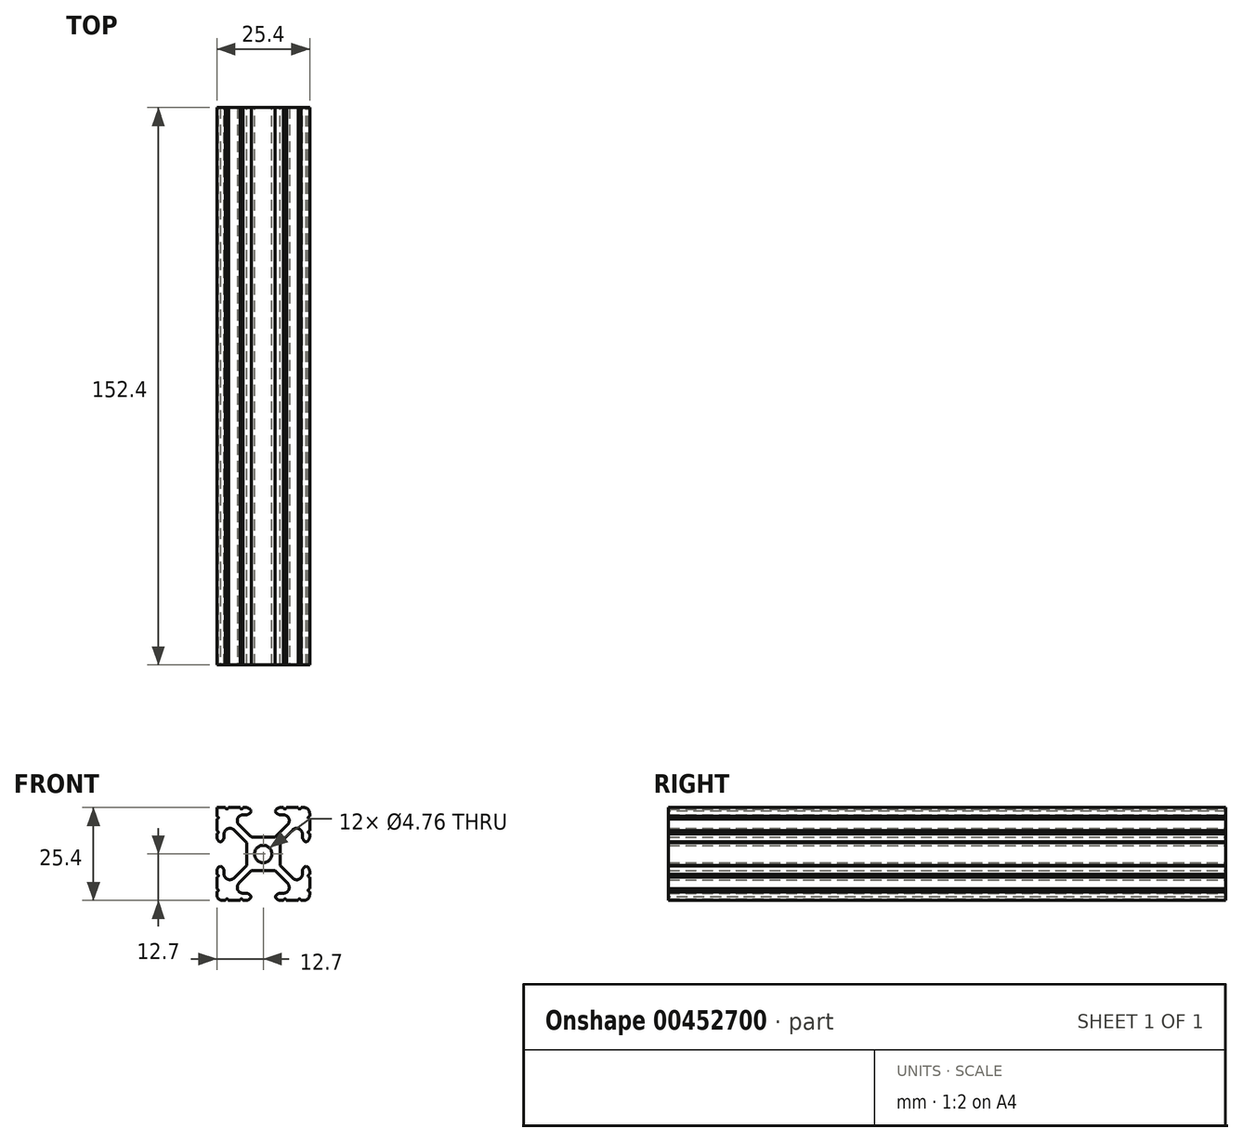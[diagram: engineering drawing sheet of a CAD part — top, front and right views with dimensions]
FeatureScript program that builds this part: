
annotation { "Feature Type Name" : "Feature", "Feature Type Description" : "" }
export const myFeature = defineFeature(function(context is Context, id is Id, definition is map)
    precondition{}
    {
        {
            var Q0;
            Q0=qCreatedBy(makeId("Front.planeOp"),FACE);
            var sketch = newSketch(context, id + "F0", { "sketchPlane" : qUnion([Q0])});
            skCircle(sketch, "E0", {"center": v(0, 0) * mm, "radius": 2.38 * mm});
            skLineSegment(sketch, "E1.bottom", {"start": v(-12.7, 12.7) * mm, "end": v(12.7, 12.7) * mm});
            skLineSegment(sketch, "E1.top", {"start": v(-12.7, -12.7) * mm, "end": v(12.7, -12.7) * mm});
            skLineSegment(sketch, "E1.left", {"start": v(-12.7, 12.7) * mm, "end": v(-12.7, -12.7) * mm});
            skLineSegment(sketch, "E1.right", {"start": v(12.7, 12.7) * mm, "end": v(12.7, -12.7) * mm});
            skPoint(sketch, "E2", {"position": v(0, 12.7) * mm});
            skLineSegment(sketch, "E3", {"start": v(0, 12.7) * mm, "end": v(-3.18, 12.7) * mm});
            skLineSegment(sketch, "E4", {"start": v(0, 12.7) * mm, "end": v(3.17, 12.7) * mm});
            skLineSegment(sketch, "E5", {"start": v(-3.18, 12.7) * mm, "end": v(-3.18, 10.72) * mm});
            skPoint(sketch, "E6", {"position": v(-12.7, 0) * mm});
            skLineSegment(sketch, "E7", {"start": v(-12.7, 0) * mm, "end": v(-12.7, 3.18) * mm});
            skLineSegment(sketch, "E8.MirrorCS", {"start": v(-12.7, 0) * mm, "end": v(-12.7, -3.18) * mm});
            skLineSegment(sketch, "E9", {"start": v(-12.7, 3.18) * mm, "end": v(-10.72, 3.18) * mm});
            skLineSegment(sketch, "E10.MirrorCS", {"start": v(-12.7, -3.18) * mm, "end": v(-10.72, -3.18) * mm});
            skLineSegment(sketch, "E11.MirrorCS", {"start": v(3.18, 12.7) * mm, "end": v(3.18, 10.72) * mm});
            skLineSegment(sketch, "E12.bottom", {"start": v(-12.7, 12.7) * mm, "end": v(-7.14, 12.7) * mm});
            skLineSegment(sketch, "E13", {"start": v(-3.18, 10.72) * mm, "end": v(-7.14, 10.72) * mm});
            skLineSegment(sketch, "E14", {"start": v(-10.72, 3.18) * mm, "end": v(-10.72, 7.14) * mm});
            skLineSegment(sketch, "E15", {"start": v(-12.7, 11.22) * mm, "end": v(-11.37, 12.7) * mm});
            skLineSegment(sketch, "E16", {"start": v(-0.7, -0.7) * mm, "end": v(-12.7, 11.22) * mm});
            skLineSegment(sketch, "E17", {"start": v(-11.37, 12.7) * mm, "end": v(0.7, 0.7) * mm});
            skLineSegment(sketch, "E18.MirrorCS", {"start": v(3.18, 10.72) * mm, "end": v(7.14, 10.72) * mm});
            skLineSegment(sketch, "E19.MirrorCS", {"start": v(10.72, 3.18) * mm, "end": v(10.72, 7.14) * mm});
            skLineSegment(sketch, "E20.MirrorCS", {"start": v(12.7, 3.18) * mm, "end": v(10.72, 3.18) * mm});
            skLineSegment(sketch, "E21.MirrorCS", {"start": v(0.7, -0.7) * mm, "end": v(12.7, 11.22) * mm});
            skLineSegment(sketch, "E22.MirrorCS", {"start": v(11.37, 12.7) * mm, "end": v(-0.7, 0.7) * mm});
            skLineSegment(sketch, "E23.MirrorCS", {"start": v(3.18, -10.72) * mm, "end": v(7.14, -10.72) * mm});
            skLineSegment(sketch, "E24.MirrorCS", {"start": v(3.18, -12.7) * mm, "end": v(3.18, -10.72) * mm});
            skLineSegment(sketch, "E25.MirrorCS", {"start": v(11.37, -12.7) * mm, "end": v(-0.7, -0.7) * mm});
            skLineSegment(sketch, "E26.MirrorCS", {"start": v(0.7, 0.7) * mm, "end": v(12.7, -11.22) * mm});
            skLineSegment(sketch, "E27.MirrorCS", {"start": v(10.72, -3.18) * mm, "end": v(10.72, -7.14) * mm});
            skLineSegment(sketch, "E28.MirrorCS", {"start": v(12.7, -3.18) * mm, "end": v(10.72, -3.18) * mm});
            skLineSegment(sketch, "E29.MirrorCS", {"start": v(-3.18, -12.7) * mm, "end": v(-3.18, -10.72) * mm});
            skLineSegment(sketch, "E30.MirrorCS", {"start": v(-3.18, -10.72) * mm, "end": v(-7.14, -10.72) * mm});
            skLineSegment(sketch, "E31.MirrorCS", {"start": v(-11.37, -12.7) * mm, "end": v(0.7, -0.7) * mm});
            skLineSegment(sketch, "E32.MirrorCS", {"start": v(-0.7, 0.7) * mm, "end": v(-12.7, -11.22) * mm});
            skLineSegment(sketch, "E33.MirrorCS", {"start": v(-10.72, -3.18) * mm, "end": v(-10.72, -7.14) * mm});
            skLineSegment(sketch, "E34.bottom", {"start": v(-4.56, 4.56) * mm, "end": v(4.56, 4.56) * mm});
            skLineSegment(sketch, "E34.top", {"start": v(-4.56, -4.56) * mm, "end": v(4.56, -4.56) * mm});
            skLineSegment(sketch, "E34.left", {"start": v(-4.56, 4.56) * mm, "end": v(-4.56, -4.56) * mm});
            skLineSegment(sketch, "E34.right", {"start": v(4.56, 4.56) * mm, "end": v(4.56, -4.56) * mm});
            skPoint(sketch, "E35", {"position": v(10.32, 12.7) * mm});
            skPoint(sketch, "E36", {"position": v(9.53, 12.7) * mm});
            skArc(sketch, "E37", {"start": v(9.53, 12.7) * mm, "mid": v(9.92, 12.3) * mm, "end": v(10.32, 12.7) * mm});
            skPoint(sketch, "E38", {"position": v(6.35, 12.7) * mm});
            skPoint(sketch, "E39", {"position": v(5.56, 12.7) * mm});
            skArc(sketch, "E40", {"start": v(5.56, 12.7) * mm, "mid": v(5.95, 12.3) * mm, "end": v(6.35, 12.7) * mm});
            skArc(sketch, "E41.MirrorCS", {"start": v(9.53, -12.7) * mm, "mid": v(9.92, -12.3) * mm, "end": v(10.32, -12.7) * mm});
            skArc(sketch, "E42.MirrorCS", {"start": v(5.56, -12.7) * mm, "mid": v(5.95, -12.3) * mm, "end": v(6.35, -12.7) * mm});
            skArc(sketch, "E43.MirrorCS", {"start": v(-5.56, -12.7) * mm, "mid": v(-5.95, -12.3) * mm, "end": v(-6.35, -12.7) * mm});
            skArc(sketch, "E44.MirrorCS", {"start": v(-9.53, -12.7) * mm, "mid": v(-9.92, -12.3) * mm, "end": v(-10.32, -12.7) * mm});
            skArc(sketch, "E45.MirrorCS", {"start": v(-5.56, 12.7) * mm, "mid": v(-5.95, 12.3) * mm, "end": v(-6.35, 12.7) * mm});
            skArc(sketch, "E46.MirrorCS", {"start": v(-9.53, 12.7) * mm, "mid": v(-9.92, 12.3) * mm, "end": v(-10.32, 12.7) * mm});
            skPoint(sketch, "E47", {"position": v(12.7, 10.32) * mm});
            skPoint(sketch, "E48", {"position": v(12.7, 9.53) * mm});
            skPoint(sketch, "E49", {"position": v(12.7, 6.35) * mm});
            skPoint(sketch, "E50", {"position": v(12.7, 5.56) * mm});
            skArc(sketch, "E51", {"start": v(12.7, 10.32) * mm, "mid": v(12.3, 9.92) * mm, "end": v(12.7, 9.53) * mm});
            skArc(sketch, "E52", {"start": v(12.7, 6.35) * mm, "mid": v(12.3, 5.95) * mm, "end": v(12.7, 5.56) * mm});
            skArc(sketch, "E53.MirrorCS", {"start": v(-12.7, 10.32) * mm, "mid": v(-12.3, 9.92) * mm, "end": v(-12.7, 9.53) * mm});
            skArc(sketch, "E54.MirrorCS", {"start": v(-12.7, 6.35) * mm, "mid": v(-12.3, 5.95) * mm, "end": v(-12.7, 5.56) * mm});
            skArc(sketch, "E55.MirrorCS", {"start": v(-12.7, -6.35) * mm, "mid": v(-12.3, -5.95) * mm, "end": v(-12.7, -5.56) * mm});
            skArc(sketch, "E56.MirrorCS", {"start": v(-12.7, -10.32) * mm, "mid": v(-12.3, -9.92) * mm, "end": v(-12.7, -9.53) * mm});
            skArc(sketch, "E57.MirrorCS", {"start": v(12.7, -6.35) * mm, "mid": v(12.3, -5.95) * mm, "end": v(12.7, -5.56) * mm});
            skArc(sketch, "E58.MirrorCS", {"start": v(12.7, -10.32) * mm, "mid": v(12.3, -9.92) * mm, "end": v(12.7, -9.53) * mm});
            skLineSegment(sketch, "E59", {"start": v(-10.72, 7.14) * mm, "end": v(-10.72, 9.25) * mm});
            skLineSegment(sketch, "E60", {"start": v(-7.14, 10.72) * mm, "end": v(-9.38, 10.72) * mm});
            skLineSegment(sketch, "E61", {"start": v(7.14, 10.72) * mm, "end": v(9.38, 10.72) * mm});
            skLineSegment(sketch, "E62", {"start": v(10.72, 7.14) * mm, "end": v(10.72, 9.25) * mm});
            skLineSegment(sketch, "E63", {"start": v(7.14, -10.72) * mm, "end": v(9.38, -10.72) * mm});
            skLineSegment(sketch, "E64", {"start": v(10.72, -7.14) * mm, "end": v(10.72, -9.25) * mm});
            skLineSegment(sketch, "E65", {"start": v(-10.72, -7.14) * mm, "end": v(-10.72, -9.25) * mm});
            skLineSegment(sketch, "E66", {"start": v(-7.14, -10.72) * mm, "end": v(-9.38, -10.72) * mm});
            skSolve(sketch);
        }
        {
            var Q0;
            {var subQ0=sQuery(id+"F0.wireOp",EDGE,"E22.MirrorCS");var subQ1=sQuery(id+"F0.wireOp",EDGE,"E0");var subQ2=makeQuery(id+"F0.imprint","INTERSECT",VERTEX,{"derivedFrom":[subQ1,subQ0]});Q0=makeQuery(id+"F0.imprint","IMPRINT",FACE,{"disambiguationData":[TD([[makeQuery(id+"F0.imprint","IMPRINT",EDGE,{"disambiguationData":[TD([[subQ2,-1.0]])],"derivedFrom":subQ1}),-1.0]])]});}
            var Q1;
            {var subQ3=sQuery(id+"F0.wireOp",EDGE,"E17");var subQ5=sQuery(id+"F0.wireOp",EDGE,"E0");var subQ6=makeQuery(id+"F0.imprint","INTERSECT",VERTEX,{"derivedFrom":[subQ5,subQ3]});Q1=makeQuery(id+"F0.imprint","IMPRINT",FACE,{"disambiguationData":[TD([[makeQuery(id+"F0.imprint","IMPRINT",EDGE,{"disambiguationData":[TD([[subQ6,-1.0]])],"derivedFrom":subQ5}),-1.0]])]});}
            var Q2;
            {var subQ0=sQuery(id+"F0.wireOp",EDGE,"E16");var subQ1=sQuery(id+"F0.wireOp",EDGE,"E0");var subQ2=makeQuery(id+"F0.imprint","INTERSECT",VERTEX,{"derivedFrom":[subQ1,subQ0]});Q2=makeQuery(id+"F0.imprint","IMPRINT",FACE,{"disambiguationData":[TD([[makeQuery(id+"F0.imprint","IMPRINT",EDGE,{"disambiguationData":[TD([[subQ2,-1.0]])],"derivedFrom":subQ1}),-1.0]])]});}
            var Q3;
            {var subQ5=sQuery(id+"F0.wireOp",EDGE,"E0");var subQ7=sQuery(id+"F0.wireOp",EDGE,"E32.MirrorCS");var subQ8=makeQuery(id+"F0.imprint","INTERSECT",VERTEX,{"derivedFrom":[subQ5,subQ7]});Q3=makeQuery(id+"F0.imprint","IMPRINT",FACE,{"disambiguationData":[TD([[makeQuery(id+"F0.imprint","IMPRINT",EDGE,{"disambiguationData":[TD([[subQ8,-1.0]])],"derivedFrom":subQ5}),-1.0]])]});}
            var Q4;
            {var subQ0=sQuery(id+"F0.wireOp",EDGE,"E31.MirrorCS");var subQ1=sQuery(id+"F0.wireOp",EDGE,"E0");var subQ2=makeQuery(id+"F0.imprint","INTERSECT",VERTEX,{"derivedFrom":[subQ1,subQ0]});Q4=makeQuery(id+"F0.imprint","IMPRINT",FACE,{"disambiguationData":[TD([[makeQuery(id+"F0.imprint","IMPRINT",EDGE,{"disambiguationData":[TD([[subQ2,-1.0]])],"derivedFrom":subQ1}),-1.0]])]});}
            var Q5;
            {var subQ3=sQuery(id+"F0.wireOp",EDGE,"E25.MirrorCS");var subQ6=sQuery(id+"F0.wireOp",EDGE,"E0");var subQ9=makeQuery(id+"F0.imprint","INTERSECT",VERTEX,{"derivedFrom":[subQ6,subQ3]});Q5=makeQuery(id+"F0.imprint","IMPRINT",FACE,{"disambiguationData":[TD([[makeQuery(id+"F0.imprint","IMPRINT",EDGE,{"disambiguationData":[TD([[subQ9,-1.0]])],"derivedFrom":subQ6}),-1.0]])]});}
            var Q6;
            {var subQ0=sQuery(id+"F0.wireOp",EDGE,"E21.MirrorCS");var subQ1=sQuery(id+"F0.wireOp",EDGE,"E0");var subQ2=makeQuery(id+"F0.imprint","INTERSECT",VERTEX,{"derivedFrom":[subQ1,subQ0]});Q6=makeQuery(id+"F0.imprint","IMPRINT",FACE,{"disambiguationData":[TD([[makeQuery(id+"F0.imprint","IMPRINT",EDGE,{"disambiguationData":[TD([[subQ2,1.0]])],"derivedFrom":subQ1}),-1.0]])]});}
            var Q7;
            {var subQ3=sQuery(id+"F0.wireOp",EDGE,"E22.MirrorCS");var subQ7=sQuery(id+"F0.wireOp",EDGE,"E0");var subQ8=makeQuery(id+"F0.imprint","INTERSECT",VERTEX,{"derivedFrom":[subQ7,subQ3]});Q7=makeQuery(id+"F0.imprint","IMPRINT",FACE,{"disambiguationData":[TD([[makeQuery(id+"F0.imprint","IMPRINT",EDGE,{"disambiguationData":[TD([[subQ8,1.0]])],"derivedFrom":subQ7}),-1.0]])]});}
            var Q8;
            {var subQ1=sQuery(id+"F0.wireOp",EDGE,"E1.right");var subQ6=sQuery(id+"F0.wireOp",EDGE,"E1.bottom");var subQ7=makeQuery(id+"F0.imprint","INTERSECT",VERTEX,{"derivedFrom":[subQ6,subQ1]});Q8=makeQuery(id+"F0.imprint","IMPRINT",FACE,{"disambiguationData":[TD([[makeQuery(id+"F0.imprint","IMPRINT",EDGE,{"disambiguationData":[TD([[subQ7,1.0]])],"derivedFrom":subQ6}),-1.0]])]});}
            var Q9;
            Q9=makeQuery(id+"F0.imprint","IMPRINT",FACE,{"disambiguationData":[TD([[makeQuery(id+"F0.imprint","IMPRINT",EDGE,{"derivedFrom":sQuery(id+"F0.wireOp",EDGE,"E19.MirrorCS")}),-1.0]])]});
            var Q10;
            {var subQ0=sQuery(id+"F0.wireOp",EDGE,"E11.MirrorCS");Q10=makeQuery(id+"F0.imprint","IMPRINT",FACE,{"disambiguationData":[TD([[makeQuery(id+"F0.imprint","IMPRINT",EDGE,{"derivedFrom":subQ0}),1.0]])]});}
            var Q11;
            {var subQ4=sQuery(id+"F0.wireOp",EDGE,"E5");Q11=makeQuery(id+"F0.imprint","IMPRINT",FACE,{"disambiguationData":[TD([[makeQuery(id+"F0.imprint","IMPRINT",EDGE,{"derivedFrom":subQ4}),-1.0]])]});}
            var Q12;
            {var subQ1=sQuery(id+"F0.wireOp",EDGE,"E15");Q12=makeQuery(id+"F0.imprint","IMPRINT",FACE,{"disambiguationData":[TD([[makeQuery(id+"F0.imprint","IMPRINT",EDGE,{"derivedFrom":subQ1}),-1.0]])]});}
            var Q13;
            {var subQ3=sQuery(id+"F0.wireOp",EDGE,"E15");Q13=makeQuery(id+"F0.imprint","IMPRINT",FACE,{"disambiguationData":[TD([[makeQuery(id+"F0.imprint","IMPRINT",EDGE,{"derivedFrom":subQ3}),1.0]])]});}
            var Q14;
            {var subQ0=sQuery(id+"F0.wireOp",EDGE,"E9");Q14=makeQuery(id+"F0.imprint","IMPRINT",FACE,{"disambiguationData":[TD([[makeQuery(id+"F0.imprint","IMPRINT",EDGE,{"derivedFrom":subQ0}),1.0]])]});}
            var Q15;
            {var subQ0=sQuery(id+"F0.wireOp",EDGE,"E10.MirrorCS");Q15=makeQuery(id+"F0.imprint","IMPRINT",FACE,{"disambiguationData":[TD([[makeQuery(id+"F0.imprint","IMPRINT",EDGE,{"derivedFrom":subQ0}),-1.0]])]});}
            var Q16;
            {var subQ0=sQuery(id+"F0.wireOp",EDGE,"E10.MirrorCS");Q16=makeQuery(id+"F0.imprint","IMPRINT",FACE,{"disambiguationData":[TD([[makeQuery(id+"F0.imprint","IMPRINT",EDGE,{"derivedFrom":subQ0}),-1.0]])]});}
            var Q17;
            {var subQ4=sQuery(id+"F0.wireOp",EDGE,"E1.top");var subQ6=sQuery(id+"F0.wireOp",EDGE,"E1.left");var subQ7=makeQuery(id+"F0.imprint","INTERSECT",VERTEX,{"derivedFrom":[subQ4,subQ6]});Q17=makeQuery(id+"F0.imprint","IMPRINT",FACE,{"disambiguationData":[TD([[makeQuery(id+"F0.imprint","IMPRINT",EDGE,{"disambiguationData":[TD([[subQ7,-1.0]])],"derivedFrom":subQ4}),1.0]])]});}
            var Q18;
            {var subQ0=sQuery(id+"F0.wireOp",EDGE,"E29.MirrorCS");Q18=makeQuery(id+"F0.imprint","IMPRINT",FACE,{"disambiguationData":[TD([[makeQuery(id+"F0.imprint","IMPRINT",EDGE,{"derivedFrom":subQ0}),1.0]])]});}
            var Q19;
            Q19=makeQuery(id+"F0.imprint","IMPRINT",FACE,{"disambiguationData":[TD([[makeQuery(id+"F0.imprint","IMPRINT",EDGE,{"derivedFrom":sQuery(id+"F0.wireOp",EDGE,"E23.MirrorCS")}),-1.0]])]});
            var Q20;
            {var subQ1=sQuery(id+"F0.wireOp",EDGE,"E1.top");var subQ6=sQuery(id+"F0.wireOp",EDGE,"E1.right");var subQ7=makeQuery(id+"F0.imprint","INTERSECT",VERTEX,{"derivedFrom":[subQ1,subQ6]});Q20=makeQuery(id+"F0.imprint","IMPRINT",FACE,{"disambiguationData":[TD([[makeQuery(id+"F0.imprint","IMPRINT",EDGE,{"disambiguationData":[TD([[subQ7,1.0]])],"derivedFrom":subQ1}),1.0]])]});}
            var Q21;
            Q21=makeQuery(id+"F0.imprint","IMPRINT",FACE,{"disambiguationData":[TD([[makeQuery(id+"F0.imprint","IMPRINT",EDGE,{"derivedFrom":sQuery(id+"F0.wireOp",EDGE,"E27.MirrorCS")}),1.0]])]});
            var Q22;
            Q22=makeQuery(id+"F0.imprint","IMPRINT",FACE,{"disambiguationData":[TD([[makeQuery(id+"F0.imprint","IMPRINT",EDGE,{"derivedFrom":sQuery(id+"F0.wireOp",EDGE,"E27.MirrorCS")}),1.0]])]});
            extrude(context, id + "F1", {"entities" : qUnion([Q0, Q1, Q2, Q3, Q4, Q5, Q6, Q7, Q8, Q9, Q10, Q11, Q12, Q13, Q14, Q15, Q16, Q17, Q18, Q19, Q20, Q21, Q22]), "depth" : 152.4 * mm});
        }
        {
            var Q0;
            Q0=makeQuery(id+"F1.opExtrude","SWEPT_EDGE",EDGE,{"disambiguationData":[OSD([sQuery(id+"F0.wireOp",EDGE,"E12.bottom"),sQuery(id+"F0.wireOp",EDGE,"E12.left")])]});
            var Q1;
            Q1=makeQuery(id+"F1.opExtrude","SWEPT_EDGE",EDGE,{"disambiguationData":[OSD([sQuery(id+"F0.wireOp",EDGE,"E1.top"),sQuery(id+"F0.wireOp",EDGE,"E1.left")])]});
            var Q2;
            Q2=makeQuery(id+"F1.opExtrude","SWEPT_EDGE",EDGE,{"disambiguationData":[OSD([sQuery(id+"F0.wireOp",EDGE,"E1.top"),sQuery(id+"F0.wireOp",EDGE,"E1.right")])]});
            var Q3;
            Q3=makeQuery(id+"F1.opExtrude","SWEPT_EDGE",EDGE,{"disambiguationData":[OSD([sQuery(id+"F0.wireOp",EDGE,"E1.bottom"),sQuery(id+"F0.wireOp",EDGE,"E1.right")])]});
            var Q4;
            Q4=makeQuery(id+"F1.opExtrude","SWEPT_EDGE",EDGE,{"disambiguationData":[OSD([sQuery(id+"F0.wireOp",EDGE,"E1.left"),sQuery(id+"F0.wireOp",EDGE,"E7"),sQuery(id+"F0.wireOp",EDGE,"E9")])]});
            var Q5;
            Q5=makeQuery(id+"F1.opExtrude","SWEPT_EDGE",EDGE,{"disambiguationData":[OSD([sQuery(id+"F0.wireOp",EDGE,"E1.left"),sQuery(id+"F0.wireOp",EDGE,"E8.MirrorCS"),sQuery(id+"F0.wireOp",EDGE,"E10.MirrorCS")])]});
            var Q6;
            Q6=makeQuery(id+"F1.opExtrude","SWEPT_EDGE",EDGE,{"disambiguationData":[OSD([sQuery(id+"F0.wireOp",EDGE,"E9"),sQuery(id+"F0.wireOp",EDGE,"E14")])]});
            var Q7;
            Q7=makeQuery(id+"F1.opExtrude","SWEPT_EDGE",EDGE,{"disambiguationData":[OSD([sQuery(id+"F0.wireOp",EDGE,"E10.MirrorCS"),sQuery(id+"F0.wireOp",EDGE,"E33.MirrorCS")])]});
            var Q8;
            Q8=makeQuery(id+"F1.opExtrude","SWEPT_EDGE",EDGE,{"disambiguationData":[OSD([sQuery(id+"F0.wireOp",EDGE,"E29.MirrorCS"),sQuery(id+"F0.wireOp",EDGE,"E30.MirrorCS")])]});
            var Q9;
            Q9=makeQuery(id+"F1.opExtrude","SWEPT_EDGE",EDGE,{"disambiguationData":[OSD([sQuery(id+"F0.wireOp",EDGE,"E1.top"),sQuery(id+"F0.wireOp",EDGE,"E29.MirrorCS")])]});
            var Q10;
            Q10=makeQuery(id+"F1.opExtrude","SWEPT_EDGE",EDGE,{"disambiguationData":[OSD([sQuery(id+"F0.wireOp",EDGE,"E1.top"),sQuery(id+"F0.wireOp",EDGE,"E24.MirrorCS")])]});
            var Q11;
            Q11=makeQuery(id+"F1.opExtrude","SWEPT_EDGE",EDGE,{"disambiguationData":[OSD([sQuery(id+"F0.wireOp",EDGE,"E23.MirrorCS"),sQuery(id+"F0.wireOp",EDGE,"E24.MirrorCS")])]});
            var Q12;
            Q12=makeQuery(id+"F1.opExtrude","SWEPT_EDGE",EDGE,{"disambiguationData":[OSD([sQuery(id+"F0.wireOp",EDGE,"E1.right"),sQuery(id+"F0.wireOp",EDGE,"E28.MirrorCS")])]});
            var Q13;
            Q13=makeQuery(id+"F1.opExtrude","SWEPT_EDGE",EDGE,{"disambiguationData":[OSD([sQuery(id+"F0.wireOp",EDGE,"E1.right"),sQuery(id+"F0.wireOp",EDGE,"E20.MirrorCS")])]});
            var Q14;
            Q14=makeQuery(id+"F1.opExtrude","SWEPT_EDGE",EDGE,{"disambiguationData":[OSD([sQuery(id+"F0.wireOp",EDGE,"E27.MirrorCS"),sQuery(id+"F0.wireOp",EDGE,"E28.MirrorCS")])]});
            var Q15;
            Q15=makeQuery(id+"F1.opExtrude","SWEPT_EDGE",EDGE,{"disambiguationData":[OSD([sQuery(id+"F0.wireOp",EDGE,"E19.MirrorCS"),sQuery(id+"F0.wireOp",EDGE,"E20.MirrorCS")])]});
            var Q16;
            Q16=makeQuery(id+"F1.opExtrude","SWEPT_EDGE",EDGE,{"disambiguationData":[OSD([sQuery(id+"F0.wireOp",EDGE,"E5"),sQuery(id+"F0.wireOp",EDGE,"E13")])]});
            var Q17;
            Q17=makeQuery(id+"F1.opExtrude","SWEPT_EDGE",EDGE,{"disambiguationData":[OSD([sQuery(id+"F0.wireOp",EDGE,"E1.bottom"),sQuery(id+"F0.wireOp",EDGE,"E3"),sQuery(id+"F0.wireOp",EDGE,"E5")])]});
            var Q18;
            Q18=makeQuery(id+"F1.opExtrude","SWEPT_EDGE",EDGE,{"disambiguationData":[OSD([sQuery(id+"F0.wireOp",EDGE,"E1.bottom"),sQuery(id+"F0.wireOp",EDGE,"E4"),sQuery(id+"F0.wireOp",EDGE,"E11.MirrorCS")])]});
            var Q19;
            Q19=makeQuery(id+"F1.opExtrude","SWEPT_EDGE",EDGE,{"disambiguationData":[OSD([sQuery(id+"F0.wireOp",EDGE,"E11.MirrorCS"),sQuery(id+"F0.wireOp",EDGE,"E18.MirrorCS")])]});
            var Q20;
            Q20=makeQuery(id+"F1.opExtrude","SWEPT_EDGE",EDGE,{"disambiguationData":[OSD([sQuery(id+"F0.wireOp",EDGE,"E12.right"),sQuery(id+"F0.wireOp",EDGE,"E17")])]});
            var Q21;
            Q21=makeQuery(id+"F1.opExtrude","SWEPT_EDGE",EDGE,{"disambiguationData":[OSD([sQuery(id+"F0.wireOp",EDGE,"E12.right"),sQuery(id+"F0.wireOp",EDGE,"E13")])]});
            var Q22;
            Q22=makeQuery(id+"F1.opExtrude","SWEPT_EDGE",EDGE,{"disambiguationData":[OSD([sQuery(id+"F0.wireOp",EDGE,"E16"),sQuery(id+"F0.wireOp",EDGE,"E59")])]});
            var Q23;
            Q23=makeQuery(id+"F1.opExtrude","SWEPT_EDGE",EDGE,{"disambiguationData":[OSD([sQuery(id+"F0.wireOp",EDGE,"E22.MirrorCS"),sQuery(id+"F0.wireOp",EDGE,"E61")])]});
            var Q24;
            Q24=makeQuery(id+"F1.opExtrude","SWEPT_EDGE",EDGE,{"disambiguationData":[OSD([sQuery(id+"F0.wireOp",EDGE,"E21.MirrorCS"),sQuery(id+"F0.wireOp",EDGE,"E62")])]});
            var Q25;
            Q25=makeQuery(id+"F1.opExtrude","SWEPT_EDGE",EDGE,{"disambiguationData":[OSD([sQuery(id+"F0.wireOp",EDGE,"E26.MirrorCS"),sQuery(id+"F0.wireOp",EDGE,"E64")])]});
            var Q26;
            Q26=makeQuery(id+"F1.opExtrude","SWEPT_EDGE",EDGE,{"disambiguationData":[OSD([sQuery(id+"F0.wireOp",EDGE,"E25.MirrorCS"),sQuery(id+"F0.wireOp",EDGE,"E63")])]});
            var Q27;
            Q27=makeQuery(id+"F1.opExtrude","SWEPT_EDGE",EDGE,{"disambiguationData":[OSD([sQuery(id+"F0.wireOp",EDGE,"E31.MirrorCS"),sQuery(id+"F0.wireOp",EDGE,"E66")])]});
            var Q28;
            Q28=makeQuery(id+"F1.opExtrude","SWEPT_EDGE",EDGE,{"disambiguationData":[OSD([sQuery(id+"F0.wireOp",EDGE,"E32.MirrorCS"),sQuery(id+"F0.wireOp",EDGE,"E65")])]});
            fillet(context, id + "F2", {"entities" : qUnion([Q0, Q1, Q2, Q3, Q4, Q5, Q6, Q7, Q8, Q9, Q10, Q11, Q12, Q13, Q14, Q15, Q16, Q17, Q18, Q19, Q20, Q21, Q22, Q23, Q24, Q25, Q26, Q27, Q28]), "radius" : 1.59 * mm, "tangentPropagation" : true, "allowEdgeOverflow" : false});
        }
    });
